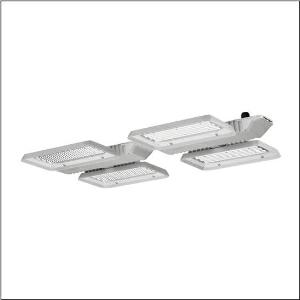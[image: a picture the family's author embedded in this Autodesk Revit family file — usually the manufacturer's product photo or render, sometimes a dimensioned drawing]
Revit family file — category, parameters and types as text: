
# Revit family: highbay_11_51hla1d24nca
name_source: partatom
category: Lighting Fixtures
units: mm (PartAtom-declared; Revit-internal decimal feet)

## family parameters
Cut with Voids When Loaded = No
Host = Face
Light Source = No
Part Type = Normal
Room Calculation Point = No
Round Connector Dimension = Use Diameter
Shared = No

## types (1)
- --- (1 x LED, 32370 lm, 189.6 W, 4000K)
    Apparent Load = 190 VA
    CIE Flux Codes = 88 95 99 100 99
    Color Rendering = 80
    Color Temperature = 4000K
    Default Elevation = 1800 mm
    Description = Highbay 11, LED high bay luminaire, primary light control with lens, of PMMA, light emission: direct distribution, primary light characteristic: symmetric, installation type: suspended mounting, surface-mounted, for 2x 2x LED, rated luminous flux: 32.370lm, luminous efficacy: 171lm/W, light colour: 840, colour temperature: 4000K, control gear: ECG DALI, with terminal, 5-pole, max. 2.5mm², mains connection: 230..240V, AC, 50/60Hz, rated input power: 190W, LED unit, of diecast aluminium, unplated, bead blasted, silver, length: 940mm, width: 500mm, height: 65mm, housing, of diecast aluminium, uncoated, bead blasted, silver, protection rating (complete): IP65, insulation class (complete): insulation class I (protective earthing), certification: CE, ENEC, VDE, UKCA, protection symbol: D, impact resistance: IK08 with glass or PC cover, permissible operating ambient temperature: -35..+45°C, reducing of maximum allowable ambient temperature of 5°C with ceiling mounting, corresponds to IFS (International Featured Standards) requirements for safety and quality in the food industry, packaging unit: 1 piece
    Height = 95 mm
    Lamp = 1 x LED
    Lamp Light Flux = 32370 lm
    Lamp Power = 189.6 W
    Lamp count = 1
    Length = 939 mm
    Luminous efficacy = 171 lm/W
    Manufacturer = Siteco
    ModVariant = No
    Model = 51HLA1D24NCA
    Mounting Place = Ceiling
    Mounting Type = Pendant
    Number of Poles = 1
    OnlyDefault = Yes
    Power Factor = 1
    Product Name = Highbay 11
    Product group = LED high bay luminaire
    ProductGroupID = 903
    Protection Class = Protection class I
    Protection Degree = IP 65
    RLX_Detail_Level = 1
    RLX_Emergency_Light_Flux = 0 lm
    RLX_Emergency_Type = 0
    RLX_Emergency_Type_DB = No
    RlxData = <blob elided: 100049 chars, md5=23acd813>
    Socket = socket
    Standby Power = 0 W
    System Light Flux = 32370 lm
    System Power = 190 W
    Type Comments = factory setting: luminous flux: 100 % | dim-lin: 254 | 535 mA
    Type Image = l_1003428.jpg
    URL = http://relux.com
    VarID = @adj_160255
    Voltage = 0 V
    Weight = 0.00 kg
    Width = 501 mm

## geometry (parser evidence)
native form markers: Blend x4, Sweep x11
no freeform markers — native parametric forms only
